# Revit family: Trim_Set-GROHE-Defined-29299_Series
name_source: partatom
category: Plumbing Fixtures
units: mm (PartAtom-declared; Revit-internal decimal feet)

## family parameters
Cut with Voids When Loaded = No
Host = Face
OmniClass Number = 23.45.05.14.17
OmniClass Title = Showers
Part Type = Normal
Room Calculation Point = No
Round Connector Dimension = Use Diameter
Shared = Yes

## types (2) — shared parameters
35110000 Pressure Balance Rough In Valve = No
35112000 Pressure Balance Rough In Valve = No
ADA Compliant = Yes
Assembly Code = D2010710
Bottom Flow Rate = 5.2 gpm
CW Connection = Yes
CWFU = 3
Cold Water Connection Diameter = 1/2"
Cold Water Connection Radius = 1/4"
Connection From Wall front To Central of pipe = 2 1/8"
Default Elevation = 44"
HW Connection = Yes
HWFU = 3
Hot Water Connection Diameter = 1"
Hot Water Connection Radius = 1/4"
Installation Type = Wall Mounted
Length = 2 3/8"
Manufacturer = Grohe
Product Documentation Link = https://americanstandard.box.com
Product Page URL = https://www.grohe.us
Revised Date = 06/06/2023
Shower Connection = Yes
Shower Connection Description = 1/2 NPT Global Shower Outlet
Shower Tempered Connection Diameter = 1/2"
Spout Connection = Yes
Spout Connection Description = 1/2 NPT Spout Global Outlet
Spout Tempered Connection Diameter = 1/2"
Tempered Water Connection = Yes
Top Flow Rate = 3.0 gpm
URL = https://www.grohe.us
Vent Connection = No
Warranty Information = Limited lifetime warranty
Waste Connection = No
Width = 3 1/8"
cUPC Compliant = Yes
zero-valued in all types: WFU

## per-type parameters (varying)
| type | Description | Finish | Material |
| 29299000 | DEFINED 2-Way Diverter Trim Starlight Chrome | Brass-Grohe-000-Starlight Chrome | Brass-Grohe-000-Starlight Chrome |
| 29299EN0 | DEFINED 2-Way Diverter Trim Brushed Nickel | Brass-Grohe-EN0-Brushed Nickel | Brass-Grohe-EN0-Brushed Nickel |

note: column(s) folded — value = type name in every type: Model

## geometry (parser evidence)
native form markers: Sweep x5
no freeform markers — native parametric forms only
